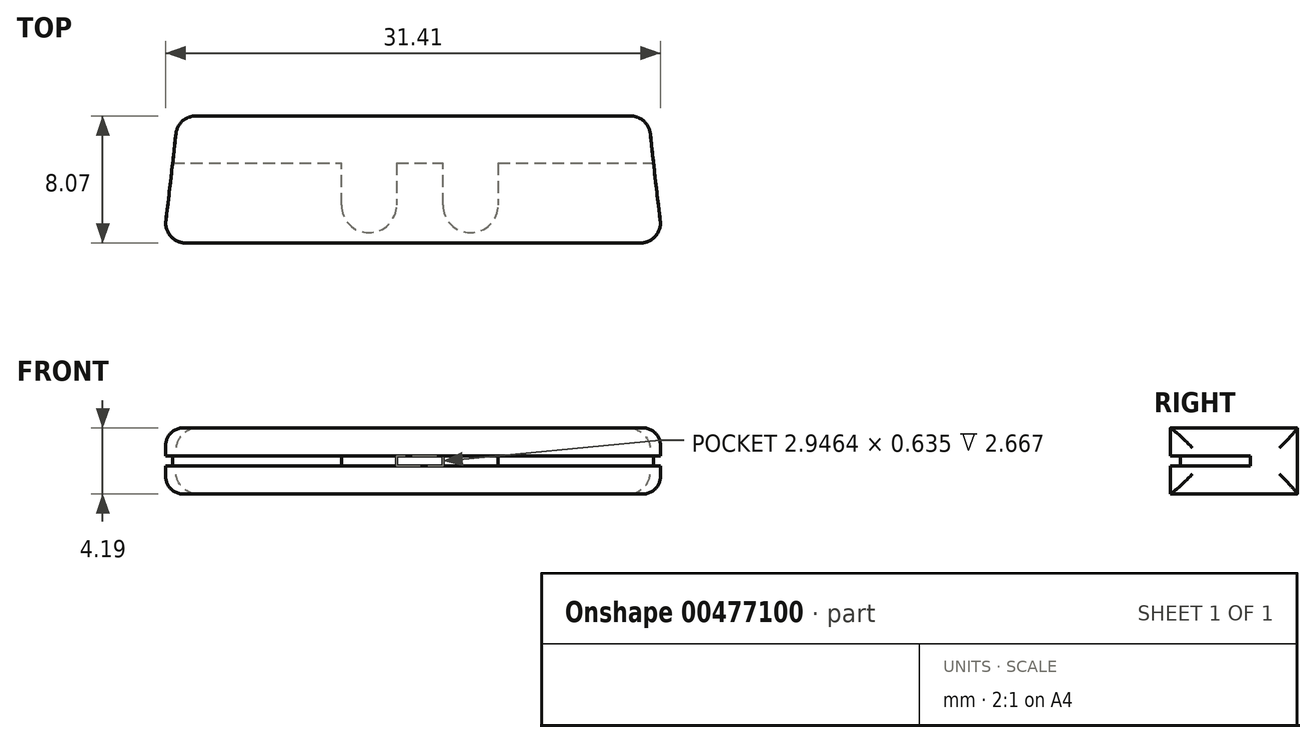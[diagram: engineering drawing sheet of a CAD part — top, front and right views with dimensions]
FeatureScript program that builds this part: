
annotation { "Feature Type Name" : "Feature", "Feature Type Description" : "" }
export const myFeature = defineFeature(function(context is Context, id is Id, definition is map)
    precondition{}
    {
        {
            var Q0;
            Q0=qCreatedBy(makeId("Top.planeOp"),FACE);
            var sketch = newSketch(context, id + "F0", { "sketchPlane" : qUnion([Q0])});
            skLineSegment(sketch, "E0.bottom", {"start": v(0, 0) * mm, "end": v(31.75, 0) * mm, "construction": true});
            skLineSegment(sketch, "E0.top", {"start": v(0, 101.6) * mm, "end": v(31.75, 101.6) * mm});
            skLineSegment(sketch, "E0.left", {"start": v(0, 0) * mm, "end": v(0, 101.6) * mm, "construction": true});
            skLineSegment(sketch, "E0.right", {"start": v(31.75, 0) * mm, "end": v(31.75, 101.6) * mm, "construction": true});
            skArc(sketch, "E1", {"start": v(0, 0) * mm, "mid": v(3.19, 50.8) * mm, "end": v(0, 101.6) * mm});
            skArc(sketch, "E2", {"start": v(31.75, 101.6) * mm, "mid": v(28.59, 50.8) * mm, "end": v(31.75, 0) * mm});
            skLineSegment(sketch, "E3", {"start": v(0, 50.8) * mm, "end": v(3.19, 50.8) * mm, "construction": true});
            skLineSegment(sketch, "E4", {"start": v(31.75, 50.8) * mm, "end": v(28.59, 50.8) * mm, "construction": true});
            skLineSegment(sketch, "E5", {"start": v(0, 0) * mm, "end": v(10.95, 0) * mm});
            skLineSegment(sketch, "E6", {"start": v(20.8, 0) * mm, "end": v(31.75, 0) * mm});
            skLineSegment(sketch, "E7", {"start": v(14.4, 0) * mm, "end": v(17.35, 0) * mm});
            skLineSegment(sketch, "E8", {"start": v(10.95, 0) * mm, "end": v(14.4, 0) * mm});
            skLineSegment(sketch, "E9", {"start": v(17.35, 0) * mm, "end": v(20.8, 0) * mm});
            skLineSegment(sketch, "E10", {"start": v(0.94, 8.07) * mm, "end": v(30.82, 8.07) * mm});
            skSolve(sketch);
        }
        {
            var Q0;
            {var subQ0=sQuery(id+"F0.wireOp",EDGE,"E5");Q0=makeQuery(id+"F0.imprint","IMPRINT",FACE,{"disambiguationData":[TD([[makeQuery(id+"F0.imprint","IMPRINT",EDGE,{"derivedFrom":subQ0}),1.0]])]});}
            extrude(context, id + "F1", {"entities" : qUnion([Q0]), "depth" : 4.2 * mm});
        }
        {
            var Q0;
            Q0=makeQuery(id+"F1.opExtrude","SWEPT_FACE",FACE,{"disambiguationData":[OSD([sQuery(id+"F0.wireOp",EDGE,"E5")])]});
            var sketch = newSketch(context, id + "F2", { "sketchPlane" : qUnion([Q0])});
            skLineSegment(sketch, "E11.bottom", {"start": v(0, 1.78) * mm, "end": v(31.75, 1.78) * mm});
            skLineSegment(sketch, "E11.top", {"start": v(0, 2.41) * mm, "end": v(31.75, 2.41) * mm});
            skLineSegment(sketch, "E11.left", {"start": v(0, 1.78) * mm, "end": v(0, 2.41) * mm});
            skLineSegment(sketch, "E11.right", {"start": v(31.75, 1.78) * mm, "end": v(31.75, 2.41) * mm});
            skLineSegment(sketch, "E12", {"start": v(0, 2.1) * mm, "end": v(31.75, 2.1) * mm, "construction": true});
            skSolve(sketch);
        }
        {
            var Q0;
            Q0=makeQuery(id+"F2.imprint","IMPRINT",FACE,{"disambiguationData":[TD([[makeQuery(id+"F2.imprint","IMPRINT",EDGE,{"derivedFrom":sQuery(id+"F2.wireOp",EDGE,"E11.bottom")}),1.0]])]});
            extrude(context, id + "F3", {"entities" : qUnion([Q0]), "operationType" : NewBodyOperationType.REMOVE, "oppositeDirection" : true, "depth" : 5.08 * mm});
        }
        {
            var Q0;
            Q0=makeQuery(id+"F1.opExtrude","CAP_FACE",FACE,{"disambiguationData":[OSD([sQuery(id+"F0.wireOp",EDGE,"E1"),sQuery(id+"F0.wireOp",EDGE,"E2"),sQuery(id+"F0.wireOp",EDGE,"t2u3qaNP-rbBg-1lCq-nUBl-GO09sGmmeMCH"),sQuery(id+"F0.wireOp",EDGE,"E5"),sQuery(id+"F0.wireOp",EDGE,"E6"),sQuery(id+"F0.wireOp",EDGE,"E7"),sQuery(id+"F0.wireOp",EDGE,"E8"),sQuery(id+"F0.wireOp",EDGE,"E9")])],"isStart":false});
            var sketch = newSketch(context, id + "F4", { "sketchPlane" : qUnion([Q0])});
            skLineSegment(sketch, "E13", {"start": v(0.6, 5.08) * mm, "end": v(31.15, 5.08) * mm, "construction": true});
            skLineSegment(sketch, "E14", {"start": v(11.32, 5.08) * mm, "end": v(11.32, 2.41) * mm});
            skLineSegment(sketch, "E15", {"start": v(11.32, 2.41) * mm, "end": v(14.83, 2.41) * mm, "construction": true});
            skLineSegment(sketch, "E16", {"start": v(14.83, 2.41) * mm, "end": v(14.83, 5.08) * mm});
            skLineSegment(sketch, "E17", {"start": v(14.83, 5.08) * mm, "end": v(17.77, 5.08) * mm});
            skLineSegment(sketch, "E18", {"start": v(17.77, 5.08) * mm, "end": v(17.77, 2.41) * mm});
            skLineSegment(sketch, "E19", {"start": v(17.77, 2.41) * mm, "end": v(21.28, 2.41) * mm, "construction": true});
            skLineSegment(sketch, "E20", {"start": v(21.28, 2.41) * mm, "end": v(21.28, 5.08) * mm});
            skLineSegment(sketch, "E21", {"start": v(21.28, 5.08) * mm, "end": v(17.77, 5.08) * mm});
            skLineSegment(sketch, "E22", {"start": v(14.83, 5.08) * mm, "end": v(11.32, 5.08) * mm});
            skArc(sketch, "E23", {"start": v(11.32, 2.41) * mm, "mid": v(13.07, 0.66) * mm, "end": v(14.83, 2.41) * mm});
            skArc(sketch, "E24", {"start": v(17.77, 2.41) * mm, "mid": v(19.53, 0.66) * mm, "end": v(21.28, 2.41) * mm});
            skSolve(sketch);
        }
        {
            var Q0;
            Q0=makeQuery(id+"F4.imprint","IMPRINT",FACE,{"disambiguationData":[TD([[makeQuery(id+"F4.imprint","IMPRINT",EDGE,{"derivedFrom":sQuery(id+"F4.wireOp",EDGE,"E14")}),1.0]])]});
            var Q1;
            Q1=makeQuery(id+"F4.imprint","IMPRINT",FACE,{"disambiguationData":[TD([[makeQuery(id+"F4.imprint","IMPRINT",EDGE,{"derivedFrom":sQuery(id+"F4.wireOp",EDGE,"E18")}),1.0]])]});
            extrude(context, id + "F5", {"entities" : qUnion([Q0, Q1]), "operationType" : NewBodyOperationType.ADD, "oppositeDirection" : true, "depth" : 4.2 * mm});
        }
        {
            var Q0;
            Q0=makeQuery(id+"F1.opExtrude","SWEPT_EDGE",EDGE,{"disambiguationData":[OSD([sQuery(id+"F0.wireOp",EDGE,"E0.top"),sQuery(id+"F0.wireOp",EDGE,"E1")])]});
            var Q1;
            Q1=makeQuery(id+"F1.opExtrude","SWEPT_EDGE",EDGE,{"disambiguationData":[OSD([sQuery(id+"F0.wireOp",EDGE,"E0.top"),sQuery(id+"F0.wireOp",EDGE,"E2")])]});
            var Q2;
            Q2=makeQuery(id+"F1.opExtrude","CAP_EDGE",EDGE,{"disambiguationData":[OSD([sQuery(id+"F0.wireOp",EDGE,"E2")])],"isStart":false});
            var Q3;
            Q3=makeQuery(id+"F1.opExtrude","CAP_EDGE",EDGE,{"disambiguationData":[OSD([sQuery(id+"F0.wireOp",EDGE,"E1")])],"isStart":false});
            var Q4;
            Q4=makeQuery(id+"F1.opExtrude","CAP_EDGE",EDGE,{"disambiguationData":[OSD([sQuery(id+"F0.wireOp",EDGE,"E1")])],"isStart":true});
            var Q5;
            Q5=makeQuery(id+"F1.opExtrude","CAP_EDGE",EDGE,{"disambiguationData":[OSD([sQuery(id+"F0.wireOp",EDGE,"E2")])],"isStart":true});
            fillet(context, id + "F6", {"entities" : qUnion([Q0, Q1, Q2, Q3, Q4, Q5]), "radius" : 1.27 * mm, "tangentPropagation" : true, "allowEdgeOverflow" : false});
        }
    });
